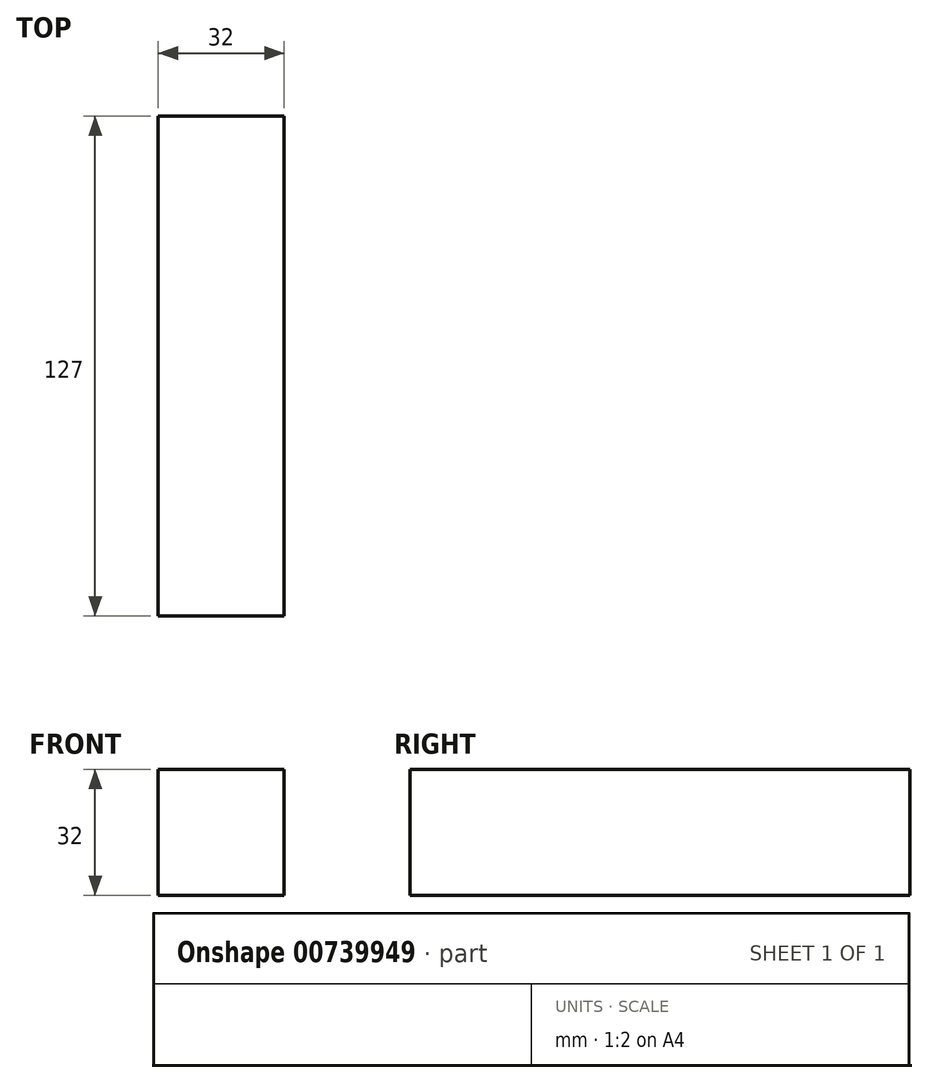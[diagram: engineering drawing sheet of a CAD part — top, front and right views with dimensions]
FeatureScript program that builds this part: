
annotation { "Feature Type Name" : "Feature", "Feature Type Description" : "" }
export const myFeature = defineFeature(function(context is Context, id is Id, definition is map)
    precondition{}
    {
        {
            var Q0;
            Q0=qCreatedBy(makeId("Front.planeOp"),FACE);
            var sketch = newSketch(context, id + "F0", { "sketchPlane" : qUnion([Q0])});
            skLineSegment(sketch, "E0.bottom", {"start": v(16, -16) * mm, "end": v(-16, -16) * mm});
            skLineSegment(sketch, "E0.top", {"start": v(16, 16) * mm, "end": v(-16, 16) * mm});
            skLineSegment(sketch, "E0.left", {"start": v(16, -16) * mm, "end": v(16, 16) * mm});
            skLineSegment(sketch, "E0.right", {"start": v(-16, -16) * mm, "end": v(-16, 16) * mm});
            skPoint(sketch, "E0.middle", {"position": v(0, 0) * mm});
            skSolve(sketch);
        }
        {
            var Q0;
            Q0=makeQuery(id+"F0.imprint","IMPRINT",FACE,{"disambiguationData":[TD([[makeQuery(id+"F0.imprint","IMPRINT",EDGE,{"derivedFrom":sQuery(id+"F0.wireOp",EDGE,"E0.bottom")}),-1.0]])]});
            extrude(context, id + "F1", {"entities" : qUnion([Q0]), "oppositeDirection" : true, "depth" : 127 * mm, "offsetDistance" : 25 * mm, "symmetric" : true});
        }
    });
